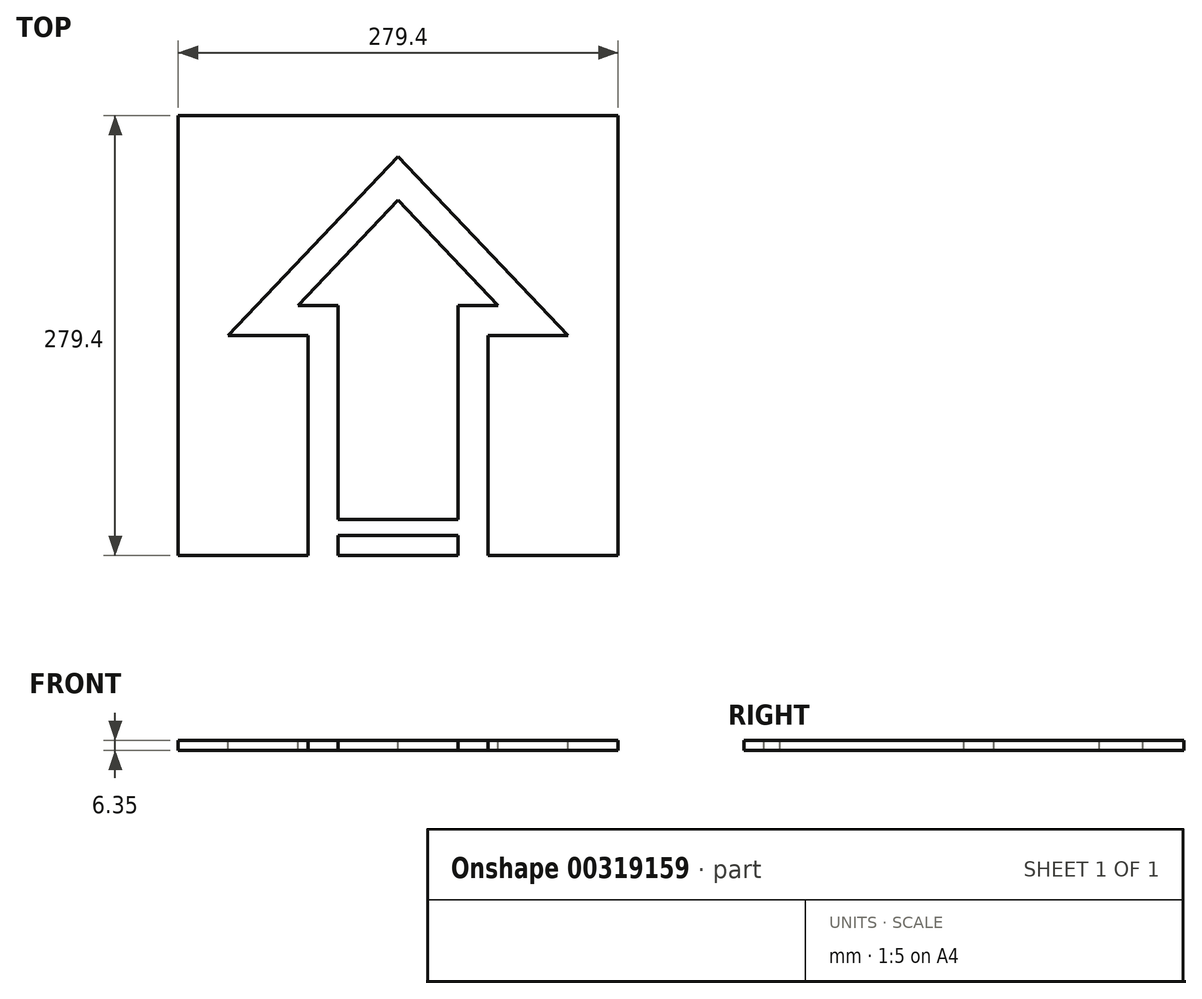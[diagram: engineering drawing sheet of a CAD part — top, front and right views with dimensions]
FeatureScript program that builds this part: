
annotation { "Feature Type Name" : "Feature", "Feature Type Description" : "" }
export const myFeature = defineFeature(function(context is Context, id is Id, definition is map)
    precondition{}
    {
        {
            var Q0;
            Q0=qCreatedBy(makeId("Top.planeOp"),FACE);
            var sketch = newSketch(context, id + "F0", { "sketchPlane" : qUnion([Q0])});
            skLineSegment(sketch, "E0.bottom", {"start": v(139.7, 139.7) * mm, "end": v(-139.7, 139.7) * mm});
            skLineSegment(sketch, "E0.top", {"start": v(139.7, -139.7) * mm, "end": v(-139.7, -139.7) * mm});
            skLineSegment(sketch, "E0.left", {"start": v(139.7, 139.7) * mm, "end": v(139.7, -139.7) * mm});
            skLineSegment(sketch, "E0.right", {"start": v(-139.7, 139.7) * mm, "end": v(-139.7, -139.7) * mm});
            skPoint(sketch, "E0.middle", {"position": v(0, 0) * mm});
            skSolve(sketch);
        }
        {
            var Q0;
            Q0 = qSketchRegion(id + "F0", true);
            extrude(context, id + "F1", {"entities" : qUnion([Q0]), "depth" : 6.35 * mm});
        }
        {
            var Q0;
            Q0=makeQuery(id+"F1.opExtrude","CAP_FACE",FACE,{"disambiguationData":[OSD([sQuery(id+"F0.wireOp",EDGE,"E0.bottom"),sQuery(id+"F0.wireOp",EDGE,"E0.top"),sQuery(id+"F0.wireOp",EDGE,"E0.left"),sQuery(id+"F0.wireOp",EDGE,"E0.right")])],"isStart":false});
            var sketch = newSketch(context, id + "F2", { "sketchPlane" : qUnion([Q0])});
            skLineSegment(sketch, "E1", {"start": v(107.95, 0) * mm, "end": v(57.15, 0) * mm});
            skLineSegment(sketch, "E2", {"start": v(57.15, 0) * mm, "end": v(57.15, -139.7) * mm});
            skLineSegment(sketch, "E3", {"start": v(-57.15, 0) * mm, "end": v(-57.15, -139.7) * mm});
            skLineSegment(sketch, "E4", {"start": v(-57.15, -139.7) * mm, "end": v(57.15, -139.7) * mm});
            skLineSegment(sketch, "E5.bottom", {"start": v(-38.1, -139.7) * mm, "end": v(38.1, -139.7) * mm});
            skLineSegment(sketch, "E5.top", {"start": v(-38.1, 0) * mm, "end": v(38.1, 0) * mm});
            skLineSegment(sketch, "E5.left", {"start": v(-38.1, -139.7) * mm, "end": v(-38.1, 0) * mm});
            skLineSegment(sketch, "E5.right", {"start": v(38.1, -139.7) * mm, "end": v(38.1, 0) * mm});
            skLineSegment(sketch, "E6", {"start": v(-38.1, -127) * mm, "end": v(38.1, -127) * mm});
            skLineSegment(sketch, "E7", {"start": v(-38.1, -116.84) * mm, "end": v(38.1, -116.84) * mm});
            skLineSegment(sketch, "E8", {"start": v(-57.15, 0) * mm, "end": v(-107.95, 0) * mm});
            skLineSegment(sketch, "E9", {"start": v(-107.95, 0) * mm, "end": v(0, 113.56) * mm});
            skLineSegment(sketch, "E10", {"start": v(0, 113.56) * mm, "end": v(107.95, 0) * mm});
            skLineSegment(sketch, "E11", {"start": v(-38.1, 0) * mm, "end": v(-38.1, 19.05) * mm});
            skLineSegment(sketch, "E12", {"start": v(38.1, 0) * mm, "end": v(38.1, 19.05) * mm});
            skLineSegment(sketch, "E13", {"start": v(-38.1, 19.05) * mm, "end": v(-63.56, 19.05) * mm});
            skLineSegment(sketch, "E14", {"start": v(-63.56, 19.05) * mm, "end": v(0, 85.91) * mm});
            skLineSegment(sketch, "E15", {"start": v(38.1, 19.05) * mm, "end": v(63.56, 19.05) * mm});
            skLineSegment(sketch, "E16", {"start": v(0, 85.91) * mm, "end": v(63.56, 19.05) * mm});
            skSolve(sketch);
        }
        {
            var Q0;
            Q0=makeQuery(id+"F2.imprint","IMPRINT",FACE,{"disambiguationData":[TD([[makeQuery(id+"F2.imprint","IMPRINT",EDGE,{"derivedFrom":sQuery(id+"F2.wireOp",EDGE,"chAg9l3B-rZNf-AvDF-Dbup-FxaLlwAwTqvq")}),-1.0]])]});
            var Q1;
            Q1=makeQuery(id+"F2.imprint","IMPRINT",FACE,{"disambiguationData":[TD([[makeQuery(id+"F2.imprint","IMPRINT",EDGE,{"derivedFrom":sQuery(id+"F2.wireOp",EDGE,"E1")}),-1.0]])]});
            var Q2;
            {var subQ0=sQuery(id+"F2.wireOp",EDGE,"E5.bottom");Q2=makeQuery(id+"F2.imprint","IMPRINT",FACE,{"disambiguationData":[TD([[makeQuery(id+"F2.imprint","IMPRINT",EDGE,{"derivedFrom":subQ0}),-1.0]])]});}
            var Q3;
            {var subQ0=sQuery(id+"F2.wireOp",EDGE,"E6");Q3=makeQuery(id+"F2.imprint","IMPRINT",FACE,{"disambiguationData":[TD([[makeQuery(id+"F2.imprint","IMPRINT",EDGE,{"derivedFrom":subQ0}),1.0]])]});}
            extrude(context, id + "F3", {"entities" : qUnion([Q0, Q1, Q2, Q3]), "operationType" : NewBodyOperationType.REMOVE, "oppositeDirection" : true, "depth" : 6.35 * mm});
        }
    });
